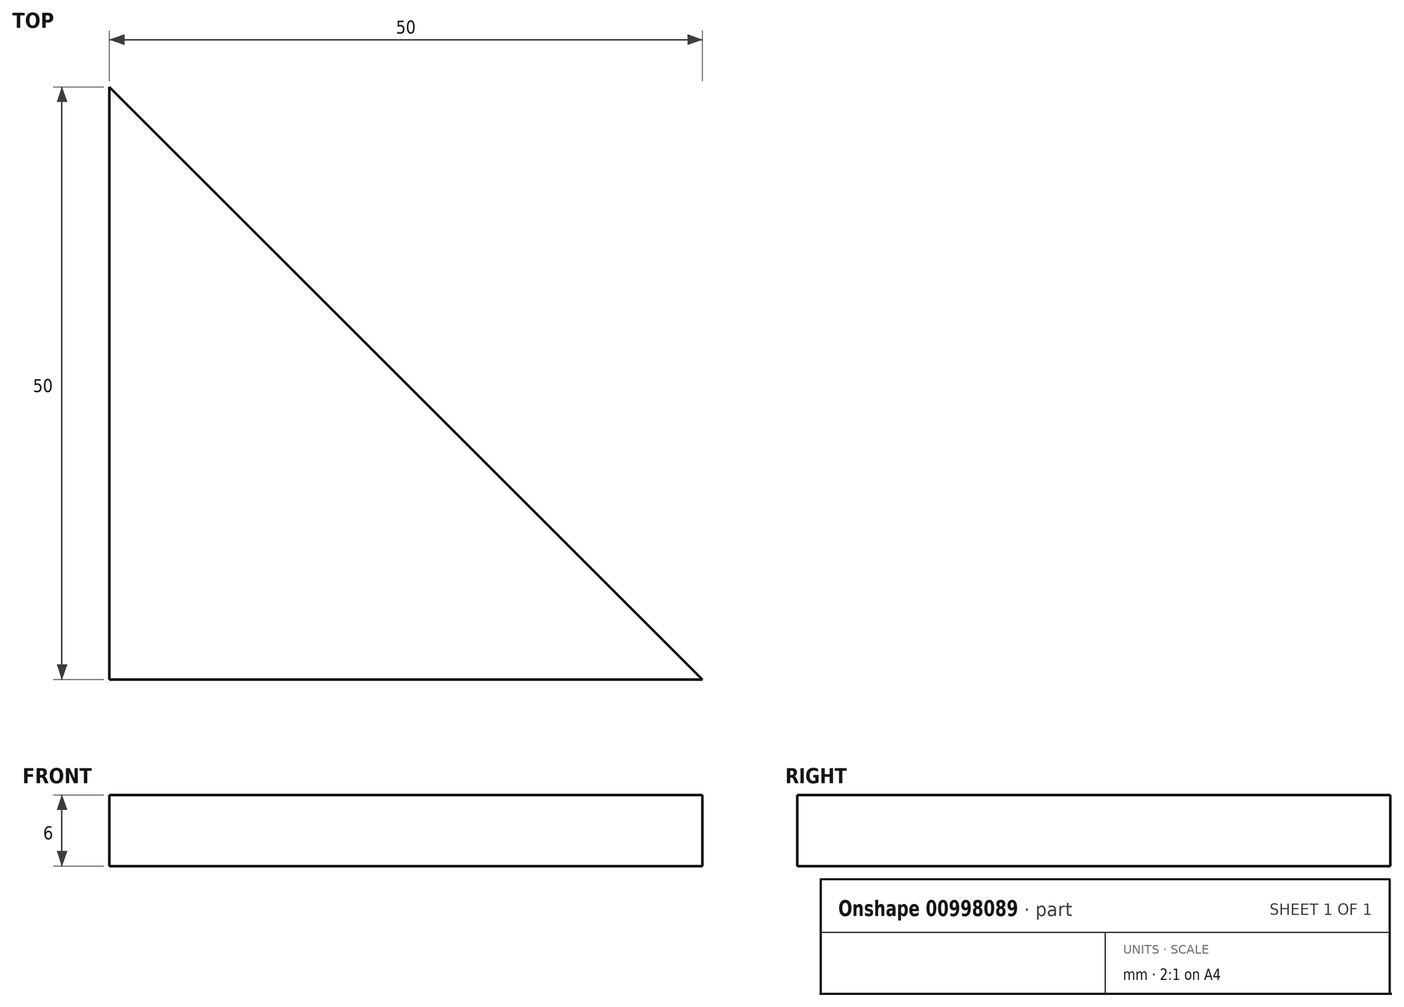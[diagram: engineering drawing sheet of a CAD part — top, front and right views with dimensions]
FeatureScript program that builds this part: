
annotation { "Feature Type Name" : "Feature", "Feature Type Description" : "" }
export const myFeature = defineFeature(function(context is Context, id is Id, definition is map)
    precondition{}
    {
        {
            var Q0;
            Q0=qCreatedBy(makeId("Top.planeOp"),FACE);
            var sketch = newSketch(context, id + "F0", { "sketchPlane" : qUnion([Q0])});
            skLineSegment(sketch, "E0", {"start": v(0, 0) * mm, "end": v(0, 50) * mm});
            skLineSegment(sketch, "E1", {"start": v(0, 50) * mm, "end": v(50, 0) * mm});
            skLineSegment(sketch, "E2", {"start": v(50, 0) * mm, "end": v(0, 0) * mm});
            skSolve(sketch);
        }
        {
            var Q0;
            Q0 = qSketchRegion(id + "F0", true);
            extrude(context, id + "F1", {"entities" : qUnion([Q0]), "depth" : 6 * mm, "offsetDistance" : 25 * mm});
        }
    });
